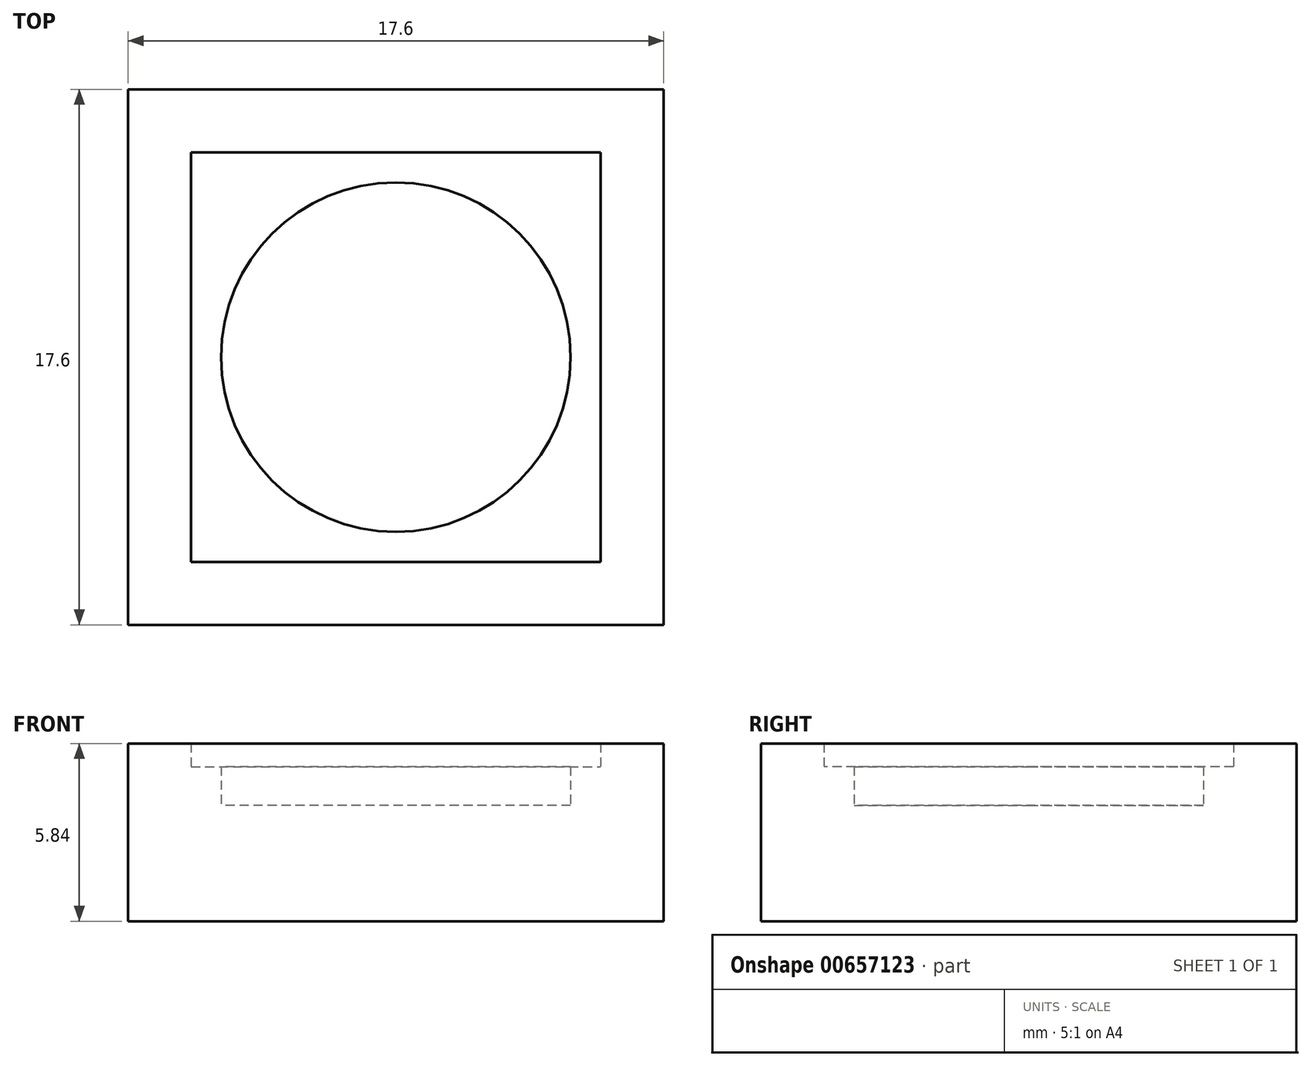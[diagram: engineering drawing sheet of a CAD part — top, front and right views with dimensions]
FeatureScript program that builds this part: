
annotation { "Feature Type Name" : "Feature", "Feature Type Description" : "" }
export const myFeature = defineFeature(function(context is Context, id is Id, definition is map)
    precondition{}
    {
        {
            var Q0;
            Q0=qCreatedBy(makeId("Top.planeOp"),FACE);
            var sketch = newSketch(context, id + "F0", { "sketchPlane" : qUnion([Q0])});
            skLineSegment(sketch, "E0.bottom", {"start": v(-8.8, 8.8) * mm, "end": v(8.8, 8.8) * mm});
            skLineSegment(sketch, "E0.top", {"start": v(-8.8, -8.8) * mm, "end": v(8.8, -8.8) * mm});
            skLineSegment(sketch, "E0.left", {"start": v(-8.8, 8.8) * mm, "end": v(-8.8, -8.8) * mm});
            skLineSegment(sketch, "E0.right", {"start": v(8.8, 8.8) * mm, "end": v(8.8, -8.8) * mm});
            skPoint(sketch, "E0.middle", {"position": v(0, 0) * mm});
            skLineSegment(sketch, "E1.bottom", {"start": v(-6.73, 6.73) * mm, "end": v(6.73, 6.73) * mm});
            skLineSegment(sketch, "E1.top", {"start": v(-6.73, -6.73) * mm, "end": v(6.73, -6.73) * mm});
            skLineSegment(sketch, "E1.left", {"start": v(-6.73, 6.73) * mm, "end": v(-6.73, -6.73) * mm});
            skLineSegment(sketch, "E1.right", {"start": v(6.73, 6.73) * mm, "end": v(6.73, -6.73) * mm});
            skCircle(sketch, "E2", {"center": v(0, 0) * mm, "radius": 5.74 * mm});
            skSolve(sketch);
        }
        {
            var Q0;
            Q0=makeQuery(id+"F0.imprint","IMPRINT",FACE,{"disambiguationData":[TD([[makeQuery(id+"F0.imprint","IMPRINT",EDGE,{"derivedFrom":sQuery(id+"F0.wireOp",EDGE,"E1.bottom")}),-1.0]])]});
            extrude(context, id + "F1", {"entities" : qUnion([Q0]), "depth" : 5.08 * mm, "offsetDistance" : 25.4 * mm});
        }
        {
            var Q0;
            Q0=makeQuery(id+"F0.imprint","IMPRINT",FACE,{"disambiguationData":[TD([[makeQuery(id+"F0.imprint","IMPRINT",EDGE,{"derivedFrom":sQuery(id+"F0.wireOp",EDGE,"E0.bottom")}),-1.0]])]});
            extrude(context, id + "F2", {"entities" : qUnion([Q0]), "operationType" : NewBodyOperationType.ADD, "depth" : 5.84 * mm, "offsetDistance" : 25.4 * mm});
        }
        {
            var Q0;
            Q0=makeQuery(id+"F0.imprint","IMPRINT",FACE,{"disambiguationData":[TD([[makeQuery(id+"F0.imprint","IMPRINT",EDGE,{"derivedFrom":sQuery(id+"F0.wireOp",EDGE,"E2")}),1.0]])]});
            extrude(context, id + "F3", {"entities" : qUnion([Q0]), "operationType" : NewBodyOperationType.ADD, "depth" : 3.8 * mm, "offsetDistance" : 25.4 * mm});
        }
    });
